# Revit family: Нижнее подключение прямое
name_source: partatom
category: Арматура трубопроводов
revit_build: Autodesk Revit 2017 (Build: 20171027_0315(x64)
units: mm (PartAtom-declared; Revit-internal decimal feet)

## family parameters
Всегда вертикально = Да
На основе рабочей плоскости = Нет
Общий = Нет
При загрузке вырезать с полостями = Нет
Размер круглого соединителя = Использовать радиус
Тип детали = Вставляется

## types (2) — shared parameters
ADSK_Единица измерения = шт
ADSK_Завод-изготовитель = Meibes
ADSK_Наименование = Узел нижнего подключения для двухтрубных систем прямой
DN1 = 20 мм
H = 48 мм
L = 50 мм
R1 = 10 мм
URL = http://www.meibes.ru
Группа модели = Узел нижнего подключения для двухтрубных систем прямой
Изготовитель = Meibes
Материал полимера = Фильтр_Черный
Материал стальной части = Сталь
Материал фитинга = РВК_Полипропилен PPR
Разработчик = ООО ПРОРУБИМ
Разработчик (телефон) = +7(495)649-85-43
Разработчик модели (URL) = http://prorubim.com
zero-valued in all types: ADSK_Масса

## per-type parameters (varying)
| type | ADSK_Код изделия | DN2 | R2 |
| D1/50 прямой, 15НРх20НР | SX 10011 | 15 мм | 8 мм |
| D2/50 прямой, 20НРх20НР | SX 10015 | 20 мм | 10 мм |

note: column(s) folded — value = type name in every type: ADSK_Обозначение
